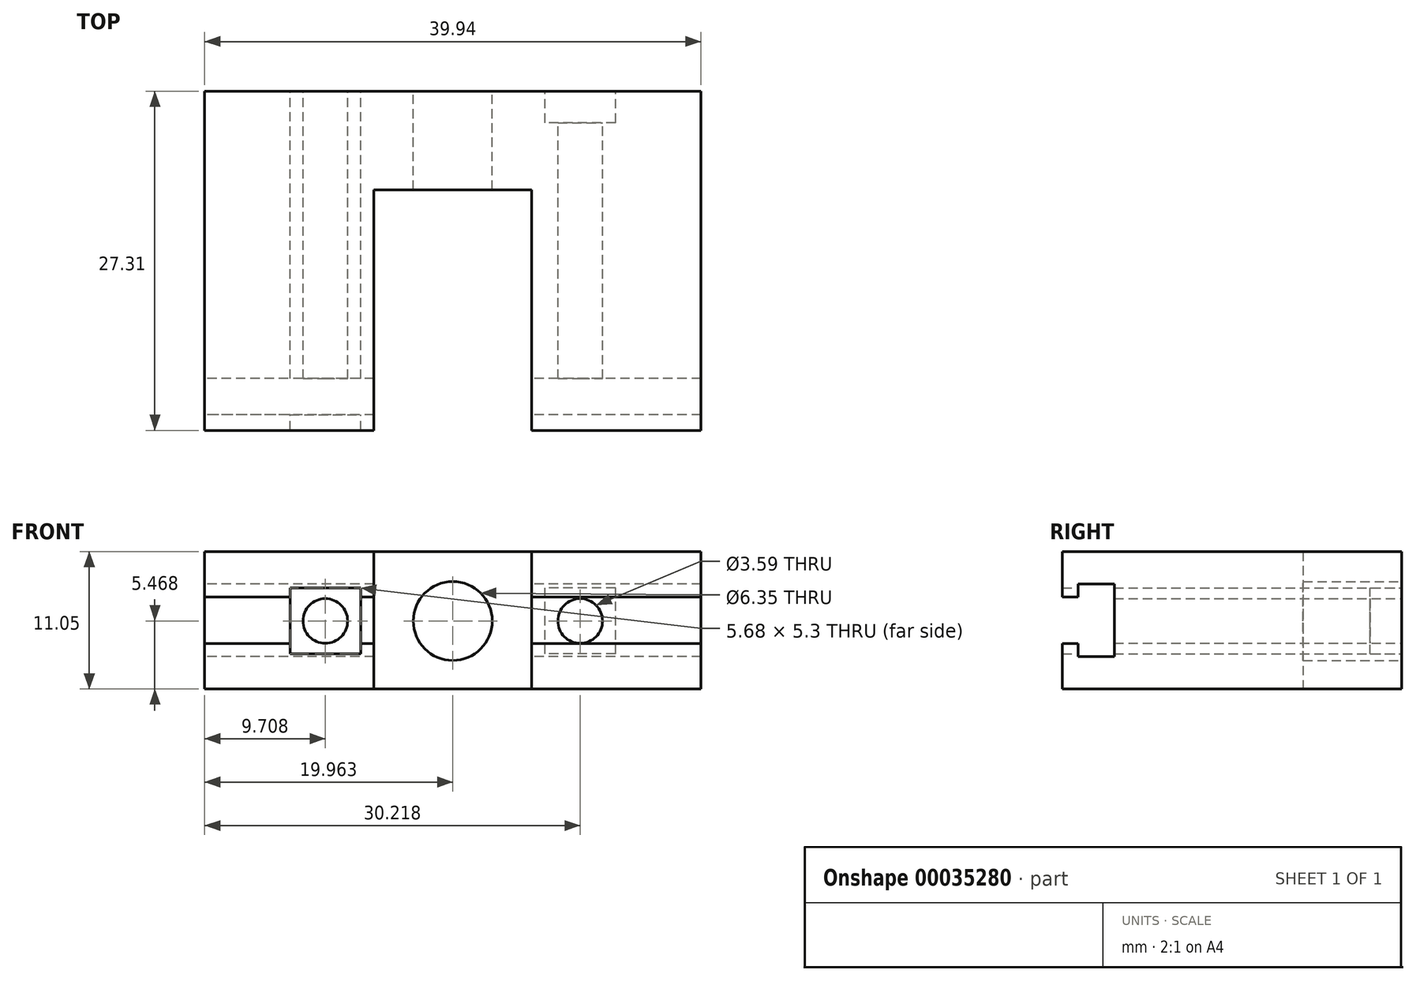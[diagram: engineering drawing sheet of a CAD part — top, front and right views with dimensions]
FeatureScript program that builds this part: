
annotation { "Feature Type Name" : "Feature", "Feature Type Description" : "" }
export const myFeature = defineFeature(function(context is Context, id is Id, definition is map)
    precondition{}
    {
        {
            var Q0;
            Q0=qCreatedBy(makeId("Top.planeOp"),FACE);
            var sketch = newSketch(context, id + "F0", { "sketchPlane" : qUnion([Q0])});
            skLineSegment(sketch, "E0.bottom", {"start": v(-17.54, 22.25) * mm, "end": v(-3.92, 22.25) * mm});
            skLineSegment(sketch, "E0.left", {"start": v(-17.54, 22.25) * mm, "end": v(-17.54, 48.3) * mm});
            skLineSegment(sketch, "E0.right", {"start": v(22.4, 22.25) * mm, "end": v(22.4, 48.3) * mm});
            skLineSegment(sketch, "E1.rect.left", {"start": v(8.78, 26.38) * mm, "end": v(8.78, 41.62) * mm});
            skLineSegment(sketch, "E1.rect.right", {"start": v(-3.92, 26.38) * mm, "end": v(-3.92, 41.62) * mm});
            skPoint(sketch, "E1.rect.middle", {"position": v(2.43, 35.27) * mm});
            skPoint(sketch, "E2.start.orphan", {"position": v(-17.54, 35.27) * mm});
            skPoint(sketch, "E3.start.orphan", {"position": v(2.43, 48.3) * mm});
            skPoint(sketch, "E4.trimOffspring.end.orphan", {"position": v(22.4, 35.27) * mm});
            skPoint(sketch, "E5.trimOffspring.end.orphan", {"position": v(2.43, 22.25) * mm});
            skLineSegment(sketch, "E6", {"start": v(8.78, 26.38) * mm, "end": v(8.78, 22.25) * mm});
            skLineSegment(sketch, "E7", {"start": v(-3.92, 26.38) * mm, "end": v(-3.92, 22.25) * mm});
            skLineSegment(sketch, "E8.trimOffspring", {"start": v(8.78, 22.25) * mm, "end": v(22.4, 22.25) * mm});
            skLineSegment(sketch, "E9", {"start": v(-17.54, 48.3) * mm, "end": v(-17.54, 49.56) * mm});
            skLineSegment(sketch, "E10", {"start": v(22.4, 48.3) * mm, "end": v(22.4, 49.56) * mm});
            skLineSegment(sketch, "E11", {"start": v(-3.92, 41.62) * mm, "end": v(8.78, 41.62) * mm});
            skPoint(sketch, "E1.rect.top.end.orphan", {"position": v(-3.92, 44.16) * mm});
            skPoint(sketch, "E12.orphan", {"position": v(8.78, 44.16) * mm});
            skLineSegment(sketch, "E13", {"start": v(-17.54, 49.56) * mm, "end": v(22.4, 49.56) * mm});
            skPoint(sketch, "E14.end.orphan", {"position": v(-17.54, 52.1) * mm});
            skSolve(sketch);
        }
        {
            var Q0;
            Q0 = qSketchRegion(id + "F0", true);
            extrude(context, id + "F1", {"entities" : qUnion([Q0]), "depth" : 11.05 * mm});
        }
        {
            var Q0;
            Q0=makeQuery(id+"F1.opExtrude","SWEPT_FACE",FACE,{"disambiguationData":[OSD([sQuery(id+"F0.wireOp",EDGE,"E0.left")])]});
            var sketch = newSketch(context, id + "F2", { "sketchPlane" : qUnion([Q0])});
            skLineSegment(sketch, "E15.rect.bottom", {"start": v(-23.52, 3.66) * mm, "end": v(-22.25, 3.66) * mm});
            skLineSegment(sketch, "E15.rect.top", {"start": v(-23.52, 7.39) * mm, "end": v(-22.25, 7.39) * mm});
            skPoint(sketch, "E15.rect.middle", {"position": v(-22.25, 5.52) * mm});
            skPoint(sketch, "E16", {"position": v(-22.25, 7.39) * mm});
            skPoint(sketch, "E17", {"position": v(-22.25, 3.66) * mm});
            skPoint(sketch, "E15.rect.right.end.orphan", {"position": v(-18.61, 7.39) * mm});
            skPoint(sketch, "E15.rect.right.start.orphan", {"position": v(-18.61, 3.66) * mm});
            skLineSegment(sketch, "E18.rect.left", {"start": v(-23.52, 2.8) * mm, "end": v(-23.52, 3.66) * mm});
            skLineSegment(sketch, "E18.rect.right", {"start": v(-26.42, 2.8) * mm, "end": v(-26.42, 8.26) * mm});
            skPoint(sketch, "E18.rect.middle", {"position": v(-24.97, 5.52) * mm});
            skPoint(sketch, "E19.orphan", {"position": v(-25.9, 3.66) * mm});
            skPoint(sketch, "E20.orphan", {"position": v(-25.9, 7.39) * mm});
            skPoint(sketch, "E21.orphan", {"position": v(-27.69, 5.52) * mm});
            skLineSegment(sketch, "E22.trimOffspring", {"start": v(-23.52, 7.39) * mm, "end": v(-23.52, 8.26) * mm});
            skLineSegment(sketch, "E23", {"start": v(-22.25, 3.66) * mm, "end": v(-22.25, 7.39) * mm});
            skLineSegment(sketch, "E24", {"start": v(-26.42, 8.26) * mm, "end": v(-26.42, 8.45) * mm});
            skLineSegment(sketch, "E25", {"start": v(-26.42, 8.45) * mm, "end": v(-23.52, 8.45) * mm});
            skLineSegment(sketch, "E26", {"start": v(-23.52, 8.26) * mm, "end": v(-23.52, 8.45) * mm});
            skLineSegment(sketch, "E27.MirrorCS", {"start": v(-26.42, 2.6) * mm, "end": v(-23.52, 2.6) * mm});
            skLineSegment(sketch, "E28.MirrorCS", {"start": v(-26.42, 2.8) * mm, "end": v(-26.42, 2.6) * mm});
            skLineSegment(sketch, "E29.MirrorCS", {"start": v(-23.52, 2.8) * mm, "end": v(-23.52, 2.6) * mm});
            skPoint(sketch, "E30.orphan", {"position": v(-26.42, 5.52) * mm});
            skSolve(sketch);
        }
        {
            var Q0;
            Q0 = qSketchRegion(id + "F2", true);
            extrude(context, id + "F3", {"entities" : qUnion([Q0]), "operationType" : NewBodyOperationType.REMOVE, "endBound" : BoundingType.THROUGH_ALL, "oppositeDirection" : true, "depth" : 25.4 * mm});
        }
        {
            var Q0;
            Q0=makeQuery(id+"F1.opExtrude","SWEPT_FACE",FACE,{"disambiguationData":[OSD([sQuery(id+"F0.wireOp",EDGE,"E13")])]});
            var sketch = newSketch(context, id + "F4", { "sketchPlane" : qUnion([Q0])});
            skPoint(sketch, "E31.start.orphan", {"position": v(-8.77, 5.47) * mm});
            skPoint(sketch, "E32.rect.middle", {"position": v(-12.68, 5.47) * mm});
            skLineSegment(sketch, "E33.MirrorCS", {"start": v(10.67, 8.12) * mm, "end": v(5, 8.12) * mm});
            skLineSegment(sketch, "E34.MirrorCS", {"start": v(10.67, 2.82) * mm, "end": v(5, 2.82) * mm});
            skLineSegment(sketch, "E35.MirrorCS", {"start": v(10.67, 2.82) * mm, "end": v(10.67, 8.12) * mm});
            skLineSegment(sketch, "E36.MirrorCS", {"start": v(5, 2.82) * mm, "end": v(5, 8.12) * mm});
            skLineSegment(sketch, "E32.rect.right", {"start": v(-9.84, 2.82) * mm, "end": v(-9.84, 8.12) * mm});
            skLineSegment(sketch, "E32.rect.left", {"start": v(-15.52, 2.82) * mm, "end": v(-15.52, 8.12) * mm});
            skLineSegment(sketch, "E32.rect.top", {"start": v(-15.52, 8.12) * mm, "end": v(-9.84, 8.12) * mm});
            skLineSegment(sketch, "E32.rect.bottom", {"start": v(-15.52, 2.82) * mm, "end": v(-9.84, 2.82) * mm});
            skCircle(sketch, "E37.MirrorC", {"center": v(7.83, 5.47) * mm, "radius": 1.8 * mm});
            skCircle(sketch, "E38", {"center": v(-12.68, 5.47) * mm, "radius": 1.8 * mm});
            skCircle(sketch, "E39", {"center": v(-2.42, 5.47) * mm, "radius": 3.18 * mm});
            skPoint(sketch, "E40.orphan", {"position": v(3.93, 5.47) * mm});
            skPoint(sketch, "E41.start.orphan", {"position": v(8.96, 5.47) * mm});
            skPoint(sketch, "E42.start.orphan", {"position": v(-2.42, 11) * mm});
            skPoint(sketch, "E41.end.orphan", {"position": v(7.69, 5.47) * mm});
            skPoint(sketch, "E43.start.orphan", {"position": v(-13.95, 5.47) * mm});
            skPoint(sketch, "E44.trimOffspring.end.orphan", {"position": v(-2.42, -0.06) * mm});
            skPoint(sketch, "E45.orphan", {"position": v(-2.43, 11.05) * mm});
            skPoint(sketch, "E46.orphan", {"position": v(-22.4, 5.52) * mm});
            skPoint(sketch, "E47.end.orphan", {"position": v(-2.43, 0) * mm});
            skPoint(sketch, "E48.trimOffspring.end.orphan", {"position": v(17.54, 5.52) * mm});
            skSolve(sketch);
        }
        {
            var Q0;
            Q0=makeQuery(id+"F4.imprint","IMPRINT",FACE,{"disambiguationData":[TD([[makeQuery(id+"F4.imprint","IMPRINT",EDGE,{"derivedFrom":sQuery(id+"F4.wireOp",EDGE,"E39")}),1.0]])]});
            var Q1;
            Q1=makeQuery(id+"F4.imprint","IMPRINT",FACE,{"disambiguationData":[TD([[makeQuery(id+"F4.imprint","IMPRINT",EDGE,{"derivedFrom":sQuery(id+"F4.wireOp",EDGE,"E38")}),1.0]])]});
            var Q2;
            Q2=makeQuery(id+"F4.imprint","IMPRINT",FACE,{"disambiguationData":[TD([[makeQuery(id+"F4.imprint","IMPRINT",EDGE,{"derivedFrom":sQuery(id+"F4.wireOp",EDGE,"E37.MirrorC")}),-1.0]])]});
            extrude(context, id + "F5", {"entities" : qUnion([Q0, Q1, Q2]), "operationType" : NewBodyOperationType.REMOVE, "endBound" : BoundingType.THROUGH_ALL, "oppositeDirection" : true, "depth" : 25.4 * mm});
        }
        {
            var Q0;
            Q0=makeQuery(id+"F4.imprint","IMPRINT",FACE,{"disambiguationData":[TD([[makeQuery(id+"F4.imprint","IMPRINT",EDGE,{"derivedFrom":sQuery(id+"F4.wireOp",EDGE,"E32.rect.right")}),1.0]])]});
            var Q1;
            Q1=makeQuery(id+"F4.imprint","IMPRINT",FACE,{"disambiguationData":[TD([[makeQuery(id+"F4.imprint","IMPRINT",EDGE,{"derivedFrom":sQuery(id+"F4.wireOp",EDGE,"E33.MirrorCS")}),1.0]])]});
            extrude(context, id + "F6", {"entities" : qUnion([Q0, Q1]), "operationType" : NewBodyOperationType.REMOVE, "oppositeDirection" : true, "depth" : 2.54 * mm});
        }
    });
